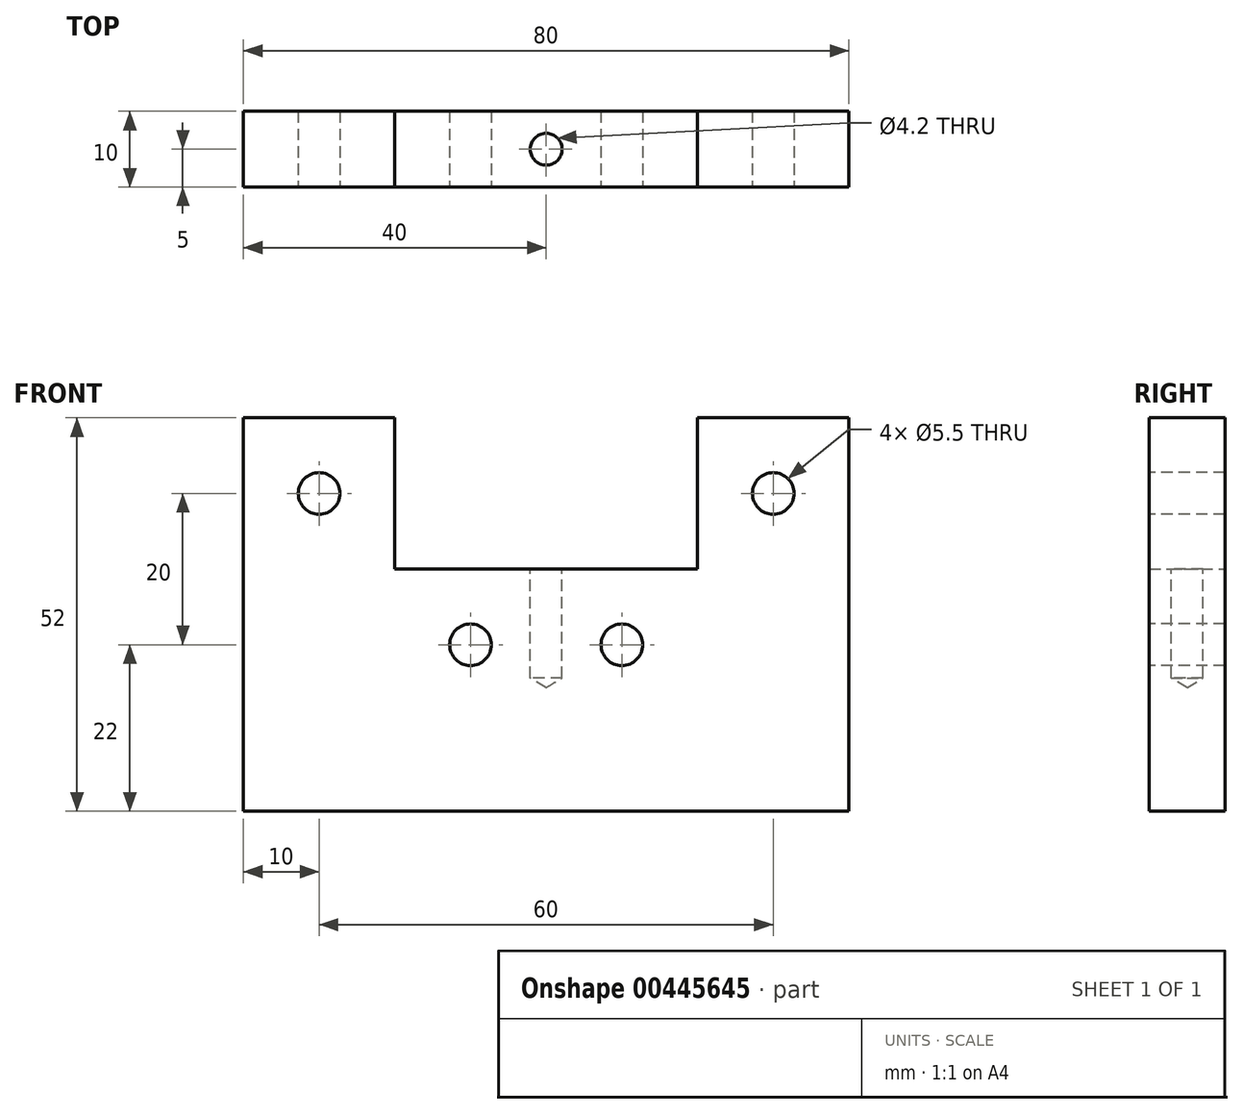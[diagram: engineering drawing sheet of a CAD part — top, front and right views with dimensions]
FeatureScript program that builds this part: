
annotation { "Feature Type Name" : "Feature", "Feature Type Description" : "" }
export const myFeature = defineFeature(function(context is Context, id is Id, definition is map)
    precondition{}
    {
        {
            var Q0;
            Q0=qCreatedBy(makeId("Front.planeOp"),FACE);
            var sketch = newSketch(context, id + "F0", { "sketchPlane" : qUnion([Q0])});
            skLineSegment(sketch, "E0.bottom", {"start": v(-40, -26) * mm, "end": v(40, -26) * mm});
            skLineSegment(sketch, "E0.top", {"start": v(-40, 26) * mm, "end": v(-20, 26) * mm});
            skLineSegment(sketch, "E0.left", {"start": v(-40, -26) * mm, "end": v(-40, 26) * mm});
            skLineSegment(sketch, "E0.right", {"start": v(40, -26) * mm, "end": v(40, 26) * mm});
            skPoint(sketch, "E0.middle", {"position": v(0, 0) * mm});
            skLineSegment(sketch, "E1.top", {"start": v(-20, 6) * mm, "end": v(20, 6) * mm});
            skLineSegment(sketch, "E1.left", {"start": v(-20, 26) * mm, "end": v(-20, 6) * mm});
            skLineSegment(sketch, "E1.right", {"start": v(20, 26) * mm, "end": v(20, 6) * mm});
            skLineSegment(sketch, "E2.trimOffspring", {"start": v(20, 26) * mm, "end": v(40, 26) * mm});
            skSolve(sketch);
        }
        {
            var Q0;
            Q0=qSketchRegion(id+"F0",true);
            extrude(context, id + "F1", {"entities" : qUnion([Q0]), "depth" : 10 * mm});
        }
        {
            var Q0;
            Q0=makeQuery(id+"F1.opExtrude","CAP_FACE",FACE,{"disambiguationData":[OSD([sQuery(id+"F0.wireOp",EDGE,"E0.bottom"),sQuery(id+"F0.wireOp",EDGE,"E0.top"),sQuery(id+"F0.wireOp",EDGE,"E0.left"),sQuery(id+"F0.wireOp",EDGE,"E0.right"),sQuery(id+"F0.wireOp",EDGE,"E1.top"),sQuery(id+"F0.wireOp",EDGE,"E1.left"),sQuery(id+"F0.wireOp",EDGE,"E1.right"),sQuery(id+"F0.wireOp",EDGE,"E2.trimOffspring")])],"isStart":false});
            var sketch = newSketch(context, id + "F2", { "sketchPlane" : qUnion([Q0])});
            skPoint(sketch, "E3", {"position": v(-30, 16) * mm});
            skPoint(sketch, "E4.MirrorP", {"position": v(30, 16) * mm});
            skPoint(sketch, "E5", {"position": v(-10, -4) * mm});
            skPoint(sketch, "E6.MirrorP", {"position": v(10, -4) * mm});
            skSolve(sketch);
        }
        {
            var Q0;
            Q0=sQuery(id+"F2.wireOp",VERTEX,"E3");
            var Q1;
            Q1=sQuery(id+"F2.wireOp",VERTEX,"E5");
            var Q2;
            Q2=sQuery(id+"F2.wireOp",VERTEX,"E6.MirrorP");
            var Q3;
            Q3=sQuery(id+"F2.wireOp",VERTEX,"E4.MirrorP");
            var Q4;
            Q4=makeQuery(id+"F1.opExtrude","SWEPT_BODY",BODY,{"disambiguationData":[OSD([sQuery(id+"F0.wireOp",EDGE,"E0.bottom"),sQuery(id+"F0.wireOp",EDGE,"E0.top"),sQuery(id+"F0.wireOp",EDGE,"E0.left"),sQuery(id+"F0.wireOp",EDGE,"E0.right"),sQuery(id+"F0.wireOp",EDGE,"E1.top"),sQuery(id+"F0.wireOp",EDGE,"E1.left"),sQuery(id+"F0.wireOp",EDGE,"E1.right"),sQuery(id+"F0.wireOp",EDGE,"E2.trimOffspring")])]});
            hole(context, id + "F3", {"style" : HoleStyle.SIMPLE, "endStyle" : HoleEndStyle.THROUGH, "standardTappedOrClearance" : lookupTablePath({ "standard" : "ISO", "fit" : "Normal", "size" : "M5", "type" : "Clearance" }), "standardBlindInLast" : lookupTablePath({ "fit" : "Standard", "standard" : "ISO", "size" : "M5", "type" : "Clearance" }), "holeDiameter" : 5.5 * mm, "tappedDepth" : 12 * mm, "tapClearance" : 3, "locations" : qUnion([Q0, Q1, Q2, Q3]), "scope" : qUnion([Q4])});
        }
        {
            var Q0;
            Q0=makeQuery(id+"F1.opExtrude","SWEPT_FACE",FACE,{"disambiguationData":[OSD([sQuery(id+"F0.wireOp",EDGE,"E1.top")])]});
            var sketch = newSketch(context, id + "F4", { "sketchPlane" : qUnion([Q0])});
            skPoint(sketch, "E7", {"position": v(0, -5) * mm});
            skPoint(sketch, "E7.positionSnap0", {"position": v(0, -10) * mm});
            skSolve(sketch);
        }
        {
            var Q0;
            Q0=sQuery(id+"F4.wireOp",VERTEX,"E7");
            var Q1;
            Q1=makeQuery(id+"F1.opExtrude","SWEPT_BODY",BODY,{"disambiguationData":[OSD([sQuery(id+"F0.wireOp",EDGE,"E0.bottom"),sQuery(id+"F0.wireOp",EDGE,"E0.top"),sQuery(id+"F0.wireOp",EDGE,"E0.left"),sQuery(id+"F0.wireOp",EDGE,"E0.right"),sQuery(id+"F0.wireOp",EDGE,"E1.top"),sQuery(id+"F0.wireOp",EDGE,"E1.left"),sQuery(id+"F0.wireOp",EDGE,"E1.right"),sQuery(id+"F0.wireOp",EDGE,"E2.trimOffspring")])]});
            hole(context, id + "F5", {"style" : HoleStyle.SIMPLE, "endStyle" : HoleEndStyle.BLIND, "standardTappedOrClearance" : lookupTablePath({ "standard" : "ISO", "engagement" : "75%", "pitch" : "0.8 mm", "size" : "M5", "type" : "Tapped" }), "standardBlindInLast" : lookupTablePath({ "standard" : "ISO", "engagement" : "75%", "pitch" : "0.8 mm", "size" : "M5", "type" : "Tapped" }), "holeDiameter" : 4.2 * mm, "showTappedDepth" : true, "holeDepth" : 14.4 * mm, "tappedDepth" : 12 * mm, "tapClearance" : 3, "locations" : qUnion([Q0]), "scope" : qUnion([Q1]), "majorDiameter" : 5 * mm});
        }
    });
